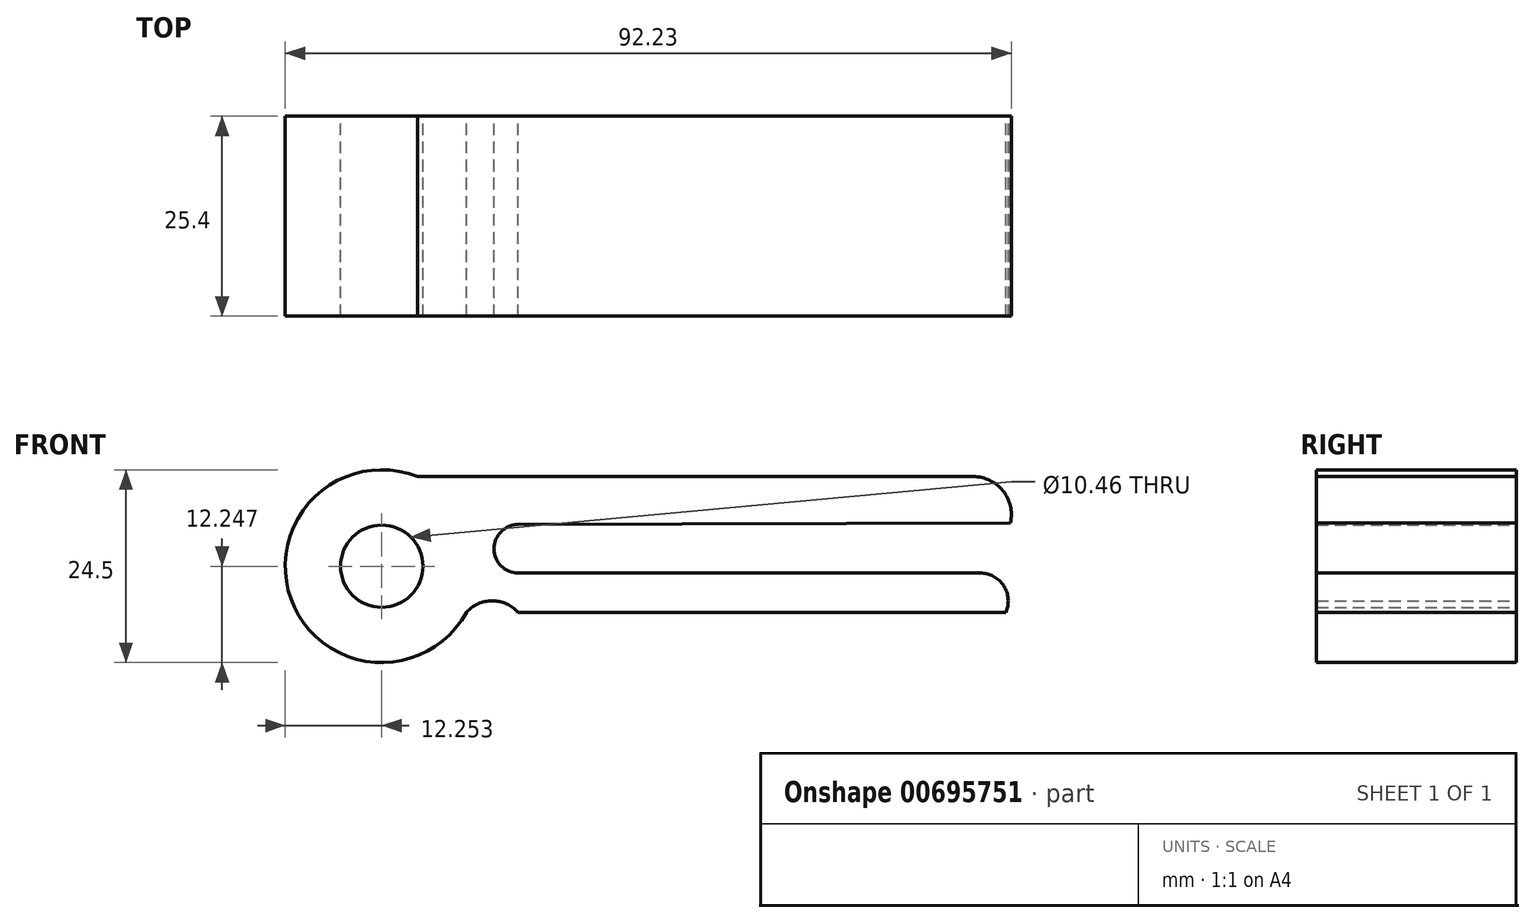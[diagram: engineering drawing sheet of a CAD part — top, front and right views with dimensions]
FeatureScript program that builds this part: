
annotation { "Feature Type Name" : "Feature", "Feature Type Description" : "" }
export const myFeature = defineFeature(function(context is Context, id is Id, definition is map)
    precondition{}
    {
        {
            var Q0;
            Q0=qCreatedBy(makeId("Front.planeOp"),FACE);
            var sketch = newSketch(context, id + "F0", { "sketchPlane" : qUnion([Q0])});
            skCircle(sketch, "E0", {"center": v(-44.19, 20.55) * mm, "radius": 5.23 * mm});
            skCircle(sketch, "E1", {"center": v(-44.19, 20.55) * mm, "radius": 12.25 * mm});
            skLineSegment(sketch, "E2", {"start": v(-39.64, 31.92) * mm, "end": v(30.98, 31.92) * mm});
            skLineSegment(sketch, "E3", {"start": v(-26.87, 25.84) * mm, "end": v(31.56, 26.05) * mm});
            skArc(sketch, "E4", {"start": v(-26.87, 25.84) * mm, "mid": v(-29.82, 25.23) * mm, "end": v(-32.3, 23.52) * mm});
            skLineSegment(sketch, "E5", {"start": v(31.56, 26.05) * mm, "end": v(35.67, 26.07) * mm});
            skArc(sketch, "E6", {"start": v(35.67, 26.07) * mm, "mid": v(34.73, 30.12) * mm, "end": v(30.98, 31.92) * mm});
            skLineSegment(sketch, "E7", {"start": v(31.86, 19.67) * mm, "end": v(-26.84, 19.67) * mm});
            skLineSegment(sketch, "E8", {"start": v(32.15, 14.68) * mm, "end": v(-26.87, 14.68) * mm});
            skArc(sketch, "E9", {"start": v(-26.87, 14.68) * mm, "mid": v(-30.15, 16.15) * mm, "end": v(-33.43, 14.68) * mm});
            skArc(sketch, "E10", {"start": v(-26.87, 25.84) * mm, "mid": v(-29.93, 22.74) * mm, "end": v(-26.84, 19.67) * mm});
            skLineSegment(sketch, "E11", {"start": v(32.15, 14.68) * mm, "end": v(35.09, 14.68) * mm});
            skArc(sketch, "E12", {"start": v(35.09, 14.68) * mm, "mid": v(34.83, 18.05) * mm, "end": v(31.86, 19.67) * mm});
            skSolve(sketch);
        }
        {
            var Q0;
            Q0 = qSketchRegion(id + "F0", true);
            extrude(context, id + "F1", {"entities" : qUnion([Q0]), "depth" : 25.4 * mm, "offsetDistance" : 25.4 * mm});
        }
    });
